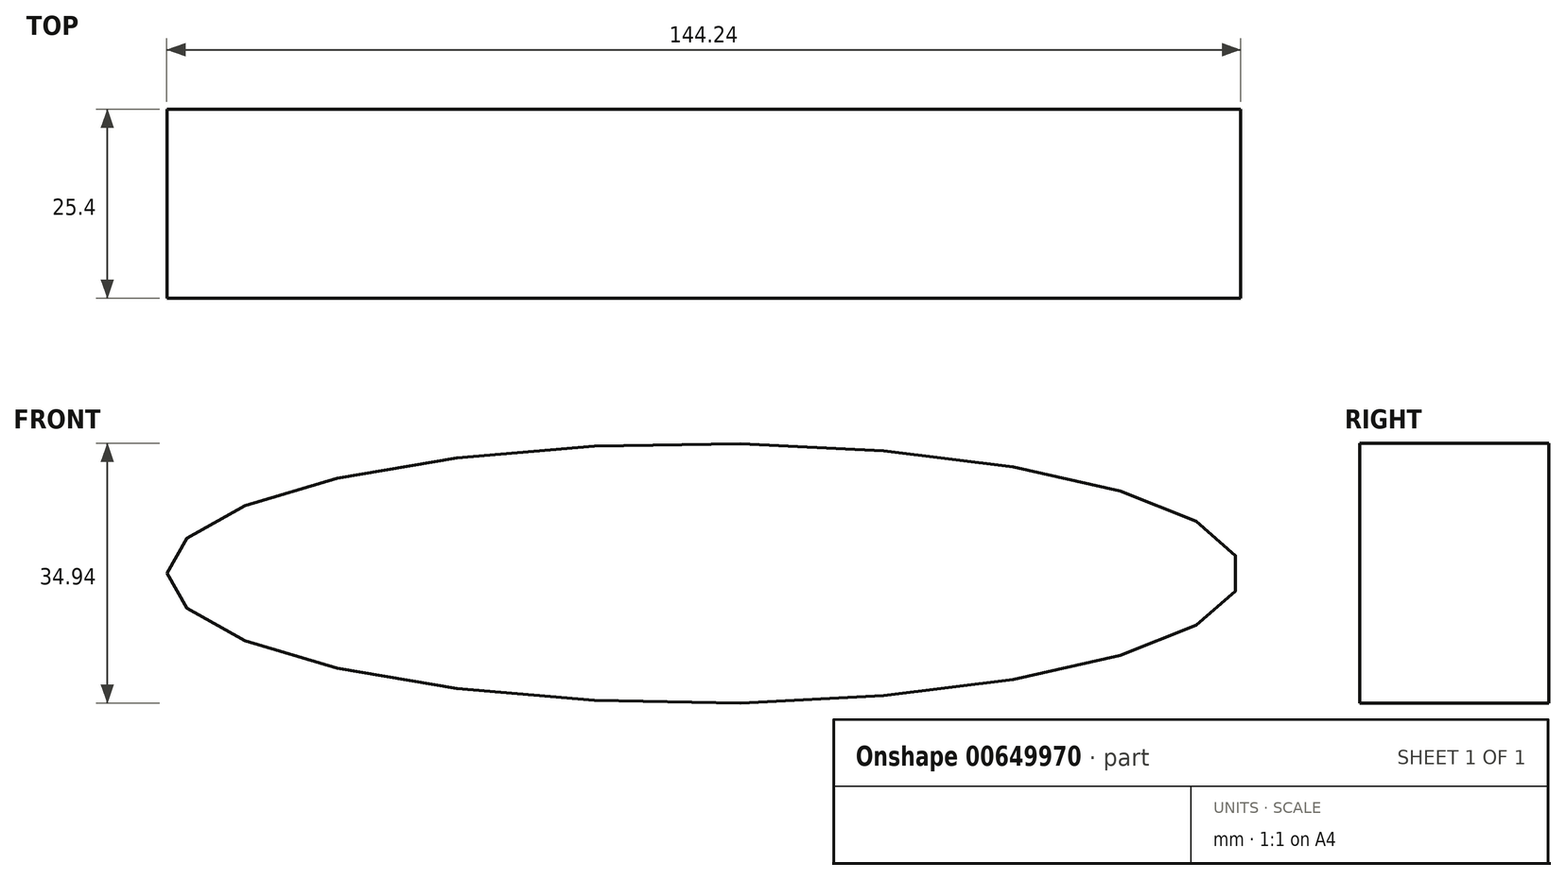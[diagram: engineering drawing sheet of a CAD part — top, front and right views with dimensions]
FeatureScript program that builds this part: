
annotation { "Feature Type Name" : "Feature", "Feature Type Description" : "" }
export const myFeature = defineFeature(function(context is Context, id is Id, definition is map)
    precondition{}
    {
        {
            var Q0;
            Q0=qCreatedBy(makeId("Front.planeOp"),FACE);
            var sketch = newSketch(context, id + "F0", { "sketchPlane" : qUnion([Q0])});
            skEllipse(sketch, "E0", {"center": v(0, 0) * mm, "majorRadius": 72.12 * mm, "minorRadius": 17.47 * mm, "majorAxis": v(-1, 0)});
            skSolve(sketch);
        }
        {
            var Q0;
            Q0=makeQuery(id+"F0.imprint","IMPRINT",FACE,{"disambiguationData":[TD([[makeQuery(id+"F0.imprint","IMPRINT",EDGE,{"derivedFrom":sQuery(id+"F0.wireOp",EDGE,"E0")}),1.0]])]});
            extrude(context, id + "F1", {"entities" : qUnion([Q0]), "depth" : 25.4 * mm, "offsetDistance" : 25.4 * mm});
        }
    });
